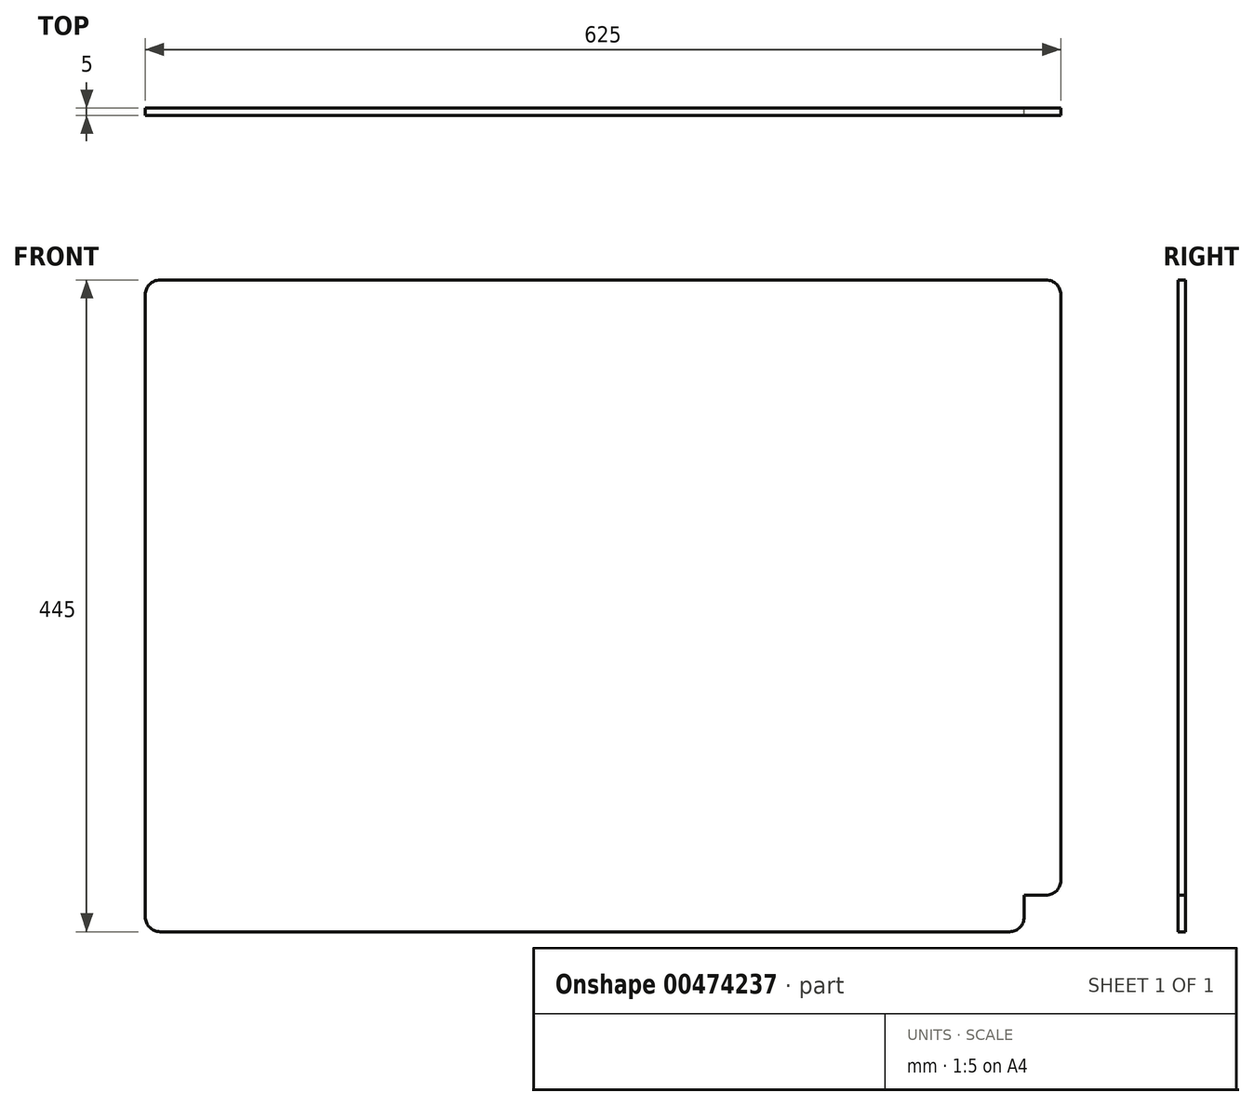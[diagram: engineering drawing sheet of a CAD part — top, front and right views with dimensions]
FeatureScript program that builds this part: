
annotation { "Feature Type Name" : "Feature", "Feature Type Description" : "" }
export const myFeature = defineFeature(function(context is Context, id is Id, definition is map)
    precondition{}
    {
        {
            var Q0;
            Q0=qCreatedBy(makeId("Front.planeOp"),FACE);
            var sketch = newSketch(context, id + "F0", { "sketchPlane" : qUnion([Q0])});
            skLineSegment(sketch, "E0.bottom", {"start": v(-291.95, 205.26) * mm, "end": v(298.05, 205.26) * mm});
            skLineSegment(sketch, "E0.top", {"start": v(-301.95, -214.74) * mm, "end": v(298.05, -214.74) * mm});
            skLineSegment(sketch, "E0.left", {"start": v(-301.95, 205.26) * mm, "end": v(-301.95, -214.74) * mm});
            skLineSegment(sketch, "E0.right", {"start": v(298.05, 205.26) * mm, "end": v(298.05, -214.74) * mm});
            skLineSegment(sketch, "E1.top", {"start": v(-291.95, -239.74) * mm, "end": v(288.05, -239.74) * mm});
            skLineSegment(sketch, "E1.left", {"start": v(-301.95, -214.74) * mm, "end": v(-301.95, -229.74) * mm});
            skLineSegment(sketch, "E1.right", {"start": v(298.05, -214.74) * mm, "end": v(298.05, -229.74) * mm});
            skLineSegment(sketch, "E2.bottom", {"start": v(-301.95, 205.26) * mm, "end": v(-301.95, 205.26) * mm});
            skLineSegment(sketch, "E2.top", {"start": v(-301.95, -214.74) * mm, "end": v(-301.95, -214.74) * mm});
            skLineSegment(sketch, "E2.right", {"start": v(-301.95, 195.26) * mm, "end": v(-301.95, -214.74) * mm});
            skLineSegment(sketch, "E3.bottom", {"start": v(298.05, 205.26) * mm, "end": v(313.05, 205.26) * mm});
            skLineSegment(sketch, "E3.top", {"start": v(298.05, -214.74) * mm, "end": v(313.05, -214.74) * mm});
            skLineSegment(sketch, "E3.right", {"start": v(323.05, 195.26) * mm, "end": v(323.05, -204.74) * mm});
            skPoint(sketch, "E4.visualSharp", {"position": v(-301.95, 205.26) * mm});
            skArc(sketch, "E4.filletArc", {"start": v(-291.95, 205.26) * mm, "mid": v(-299.02, 202.33) * mm, "end": v(-301.95, 195.26) * mm});
            skPoint(sketch, "E5.visualSharp", {"position": v(323.05, 205.26) * mm});
            skArc(sketch, "E5.filletArc", {"start": v(323.05, 195.26) * mm, "mid": v(320.12, 202.33) * mm, "end": v(313.05, 205.26) * mm});
            skPoint(sketch, "E6.visualSharp", {"position": v(323.05, -214.74) * mm});
            skArc(sketch, "E6.filletArc", {"start": v(313.05, -214.74) * mm, "mid": v(320.12, -211.81) * mm, "end": v(323.05, -204.74) * mm});
            skPoint(sketch, "E7.visualSharp", {"position": v(298.05, -239.74) * mm});
            skArc(sketch, "E7.filletArc", {"start": v(288.05, -239.74) * mm, "mid": v(295.12, -236.81) * mm, "end": v(298.05, -229.74) * mm});
            skPoint(sketch, "E8.visualSharp", {"position": v(-301.95, -239.74) * mm});
            skArc(sketch, "E8.filletArc", {"start": v(-301.95, -229.74) * mm, "mid": v(-299.02, -236.81) * mm, "end": v(-291.95, -239.74) * mm});
            skPoint(sketch, "E9", {"position": v(-17.75, 17.75) * mm});
            skPoint(sketch, "E10", {"position": v(17.75, 17.75) * mm});
            skPoint(sketch, "E11", {"position": v(-17.75, -17.75) * mm});
            skPoint(sketch, "E12", {"position": v(17.75, -17.75) * mm});
            skSolve(sketch);
        }
        {
            var Q0;
            Q0=makeQuery(id+"F0.imprint","IMPRINT",FACE,{"disambiguationData":[TD([[makeQuery(id+"F0.imprint","IMPRINT",EDGE,{"derivedFrom":sQuery(id+"F0.wireOp",EDGE,"E0.bottom")}),-1.0]])]});
            var Q1;
            Q1=makeQuery(id+"F0.imprint","IMPRINT",FACE,{"disambiguationData":[TD([[makeQuery(id+"F0.imprint","IMPRINT",EDGE,{"derivedFrom":sQuery(id+"F0.wireOp",EDGE,"E0.top")}),-1.0]])]});
            var Q2;
            Q2=makeQuery(id+"F0.imprint","IMPRINT",FACE,{"disambiguationData":[TD([[makeQuery(id+"F0.imprint","IMPRINT",EDGE,{"derivedFrom":sQuery(id+"F0.wireOp",EDGE,"E3.bottom")}),-1.0]])]});
            extrude(context, id + "F1", {"entities" : qUnion([Q0, Q1, Q2]), "depth" : 5 * mm});
        }
    });
